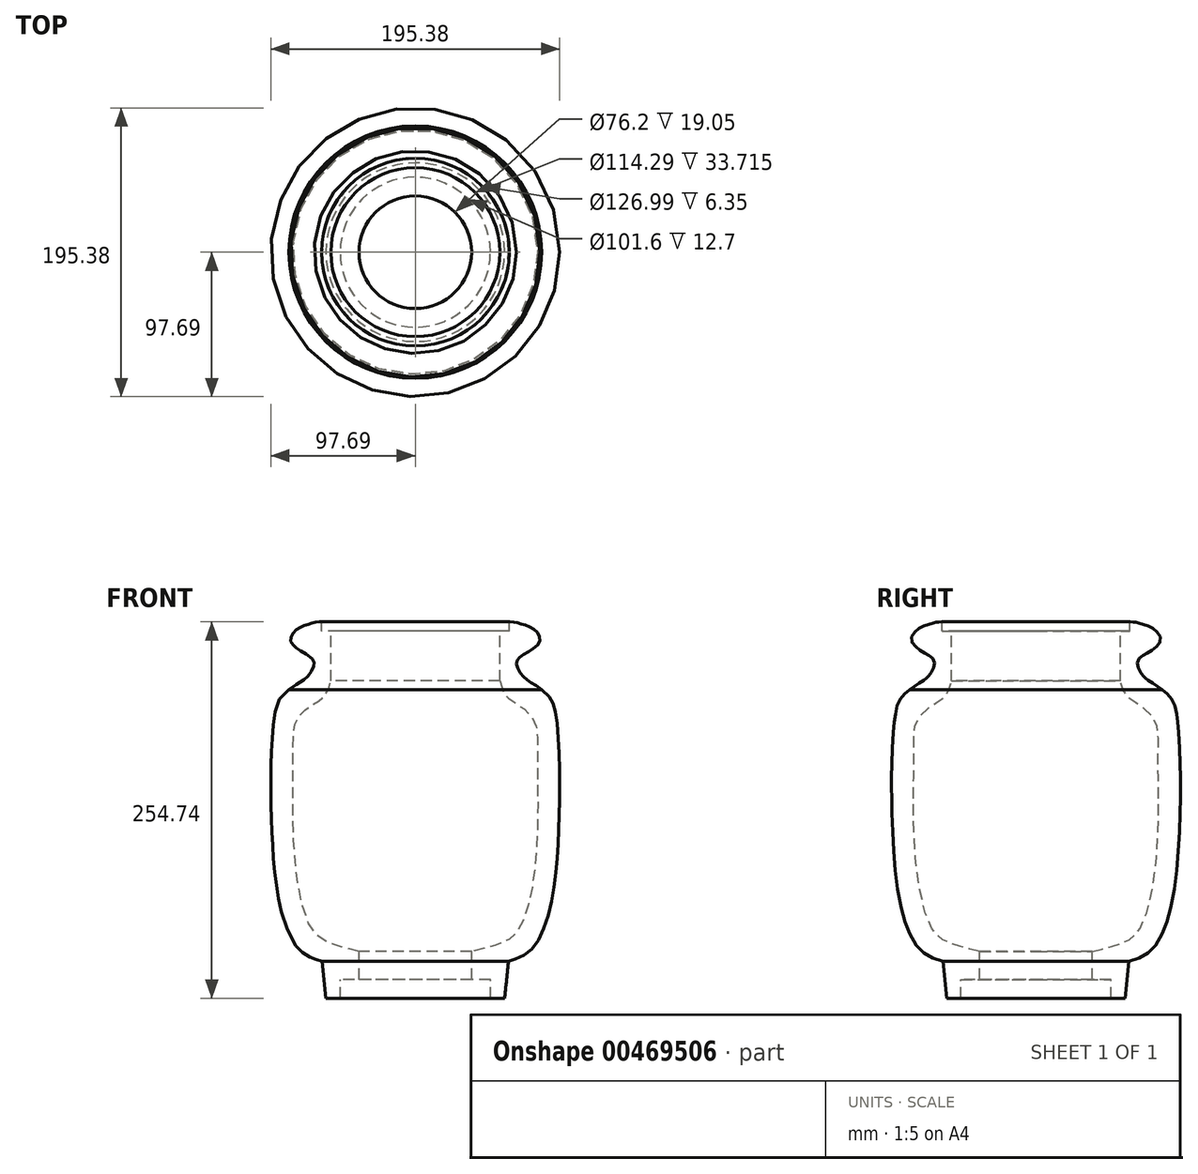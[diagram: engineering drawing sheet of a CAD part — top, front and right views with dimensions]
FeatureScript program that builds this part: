
annotation { "Feature Type Name" : "Feature", "Feature Type Description" : "" }
export const myFeature = defineFeature(function(context is Context, id is Id, definition is map)
    precondition{}
    {
        {
            var Q0;
            Q0=qCreatedBy(makeId("Front.planeOp"),FACE);
            var sketch = newSketch(context, id + "F0", { "sketchPlane" : qUnion([Q0])});
            skLineSegment(sketch, "E0", {"start": v(-38.1, 12.7) * mm, "end": v(-50.8, 12.7) * mm});
            skLineSegment(sketch, "E1", {"start": v(-50.8, 12.7) * mm, "end": v(-50.8, 0) * mm});
            skLineSegment(sketch, "E2", {"start": v(-50.8, 0) * mm, "end": v(-60.45, 0) * mm});
            skLineSegment(sketch, "E3", {"start": v(-60.45, 0) * mm, "end": v(-63, 24.85) * mm});
            skFitSpline(sketch, "E4", {"points": [v(-85.47, 208.82) * mm, v(-94.45, 195.79) * mm, v(-97.62, 152.8) * mm, v(-96.67, 106.19) * mm, v(-91.44, 62.48) * mm, v(-77.33, 31.7) * mm, v(-63, 24.85) * mm], "startDerivative": vector(-152.35, -127.25) * mm, "endDerivative": vector(97.69, -34.04) * mm});
            skLineSegment(sketch, "E5", {"start": v(-38.1, 12.7) * mm, "end": v(-38.1, 31.75) * mm});
            skFitSpline(sketch, "E6", {"points": [v(-57.15, 214.67) * mm, v(-64.64, 201.7) * mm, v(-79.3, 190.05) * mm, v(-82.65, 164.15) * mm, v(-81.94, 100.01) * mm, v(-69.15, 45.34) * mm, v(-57.73, 37.19) * mm, v(-38.1, 31.75) * mm], "startDerivative": vector(-58.43, -235.9) * mm, "endDerivative": vector(313.05, -69.63) * mm});
            skLineSegment(sketch, "E7", {"start": v(0, 215.33) * mm, "end": v(0, 0) * mm, "construction": true});
            skPoint(sketch, "E8", {"position": v(-82.65, 152.8) * mm});
            skFitSpline(sketch, "E9", {"points": [v(-85.47, 208.82) * mm, v(-73.2, 217.43) * mm, v(-68.5, 227.1) * mm, v(-73.51, 232.67) * mm, v(-84.18, 241.48) * mm, v(-80.26, 249.59) * mm, v(-70.99, 253.48) * mm, v(-63.5, 254.74) * mm], "startDerivative": vector(97.94, 76.94) * mm, "endDerivative": vector(80.77, -1.22) * mm});
            skLineSegment(sketch, "E10", {"start": v(-63.5, 254.74) * mm, "end": v(-63.5, 248.39) * mm});
            skLineSegment(sketch, "E11", {"start": v(-63.5, 248.39) * mm, "end": v(-57.15, 248.39) * mm});
            skLineSegment(sketch, "E12", {"start": v(-57.15, 248.39) * mm, "end": v(-57.15, 214.67) * mm});
            skLineSegment(sketch, "E13", {"start": v(0, 215.33) * mm, "end": v(0, -75.14) * mm});
            skSolve(sketch);
        }
        {
            var Q0;
            Q0=makeQuery(id+"F0.imprint","IMPRINT",FACE,{"disambiguationData":[TD([[makeQuery(id+"F0.imprint","IMPRINT",EDGE,{"derivedFrom":sQuery(id+"F0.wireOp",EDGE,"E0")}),-1.0]])]});
            var Q1;
            Q1=sQuery(id+"F0.wireOp",EDGE,"E7");
            revolve(context, id + "F1", {"entities" : qUnion([Q0]), "axis" : qUnion([Q1]), "revolveType" : RevolveType.FULL});
        }
    });
